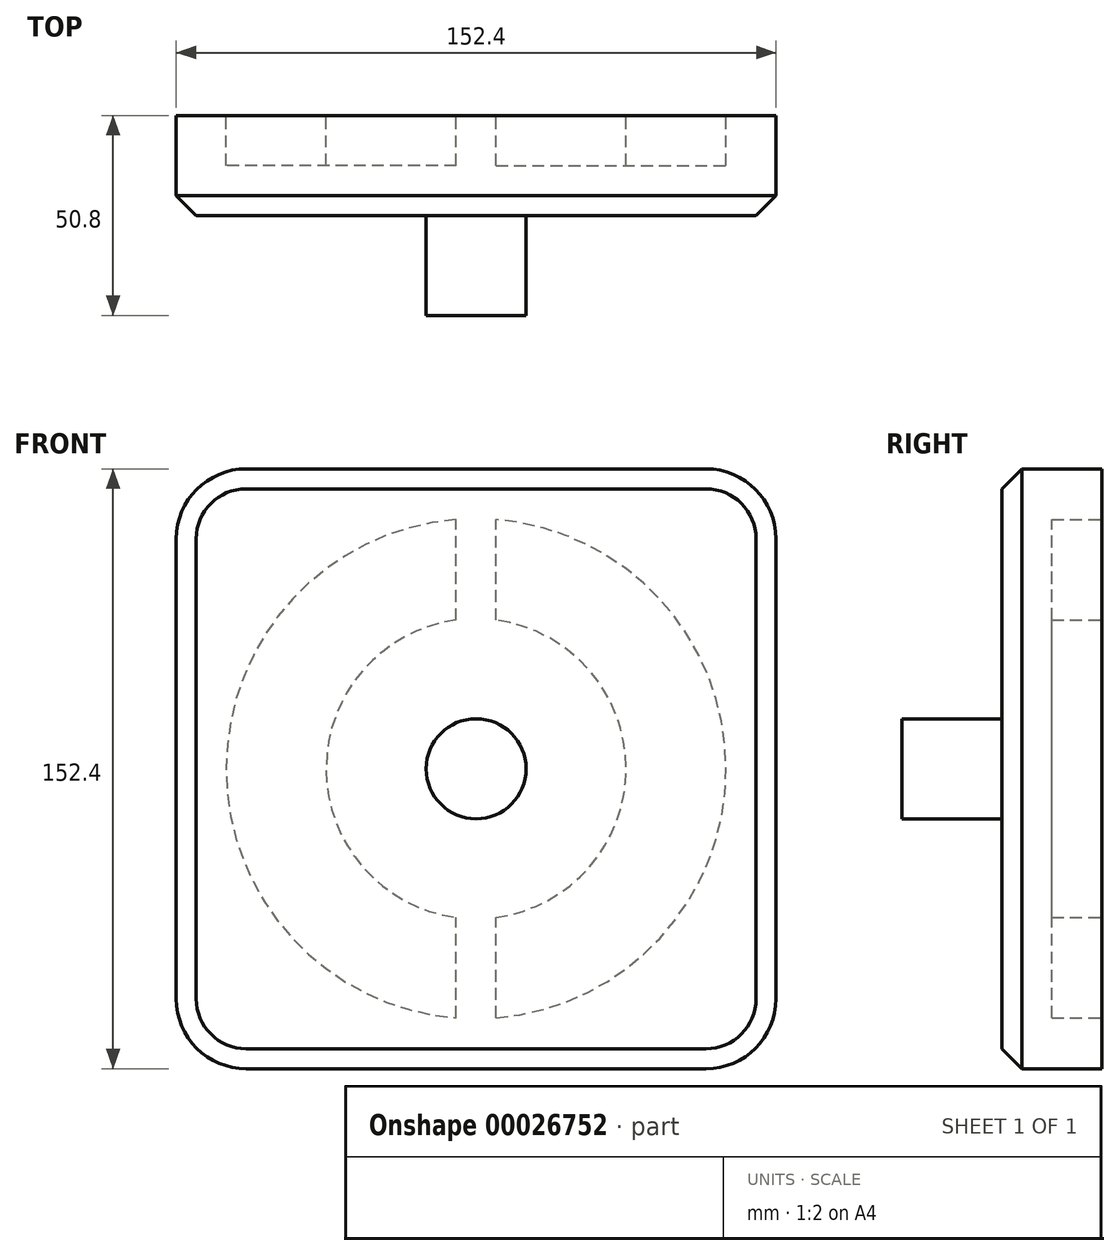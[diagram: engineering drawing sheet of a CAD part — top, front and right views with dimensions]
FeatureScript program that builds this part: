
annotation { "Feature Type Name" : "Feature", "Feature Type Description" : "" }
export const myFeature = defineFeature(function(context is Context, id is Id, definition is map)
    precondition{}
    {
        {
            var Q0;
            Q0=qCreatedBy(makeId("Front.planeOp"),FACE);
            var sketch = newSketch(context, id + "F0", { "sketchPlane" : qUnion([Q0])});
            skLineSegment(sketch, "E0.rect.bottom", {"start": v(76.2, -76.2) * mm, "end": v(-76.2, -76.2) * mm});
            skLineSegment(sketch, "E0.rect.top", {"start": v(76.2, 76.2) * mm, "end": v(-76.2, 76.2) * mm});
            skLineSegment(sketch, "E0.rect.left", {"start": v(76.2, -76.2) * mm, "end": v(76.2, 76.2) * mm});
            skLineSegment(sketch, "E0.rect.right", {"start": v(-76.2, -76.2) * mm, "end": v(-76.2, 76.2) * mm});
            skPoint(sketch, "E0.rect.middle", {"position": v(0, 0) * mm});
            skSolve(sketch);
        }
        {
            var Q0;
            Q0=makeQuery(id+"F0.imprint","IMPRINT",FACE,{"disambiguationData":[TD([[makeQuery(id+"F0.imprint","IMPRINT",EDGE,{"derivedFrom":sQuery(id+"F0.wireOp",EDGE,"E0.rect.bottom")}),-1.0]])]});
            extrude(context, id + "F1", {"entities" : qUnion([Q0]), "depth" : 25.4 * mm});
        }
        {
            var Q0;
            Q0=makeQuery(id+"F1.opExtrude","CAP_FACE",FACE,{"disambiguationData":[OSD([sQuery(id+"F0.wireOp",EDGE,"E0.rect.bottom"),sQuery(id+"F0.wireOp",EDGE,"E0.rect.top"),sQuery(id+"F0.wireOp",EDGE,"E0.rect.left"),sQuery(id+"F0.wireOp",EDGE,"E0.rect.right")])],"isStart":false});
            var sketch = newSketch(context, id + "F2", { "sketchPlane" : qUnion([Q0])});
            skCircle(sketch, "E1", {"center": v(0, 0) * mm, "radius": 12.7 * mm});
            skSolve(sketch);
        }
        {
            var Q0;
            Q0=makeQuery(id+"F2.imprint","IMPRINT",FACE,{"disambiguationData":[TD([[makeQuery(id+"F2.imprint","IMPRINT",EDGE,{"derivedFrom":sQuery(id+"F2.wireOp",EDGE,"E1")}),1.0]])]});
            extrude(context, id + "F3", {"entities" : qUnion([Q0]), "operationType" : NewBodyOperationType.ADD, "depth" : 25.4 * mm});
        }
        {
            var Q0;
            Q0=makeQuery(id+"F1.opExtrude","SWEPT_EDGE",EDGE,{"disambiguationData":[OSD([sQuery(id+"F0.wireOp",EDGE,"E0.rect.top"),sQuery(id+"F0.wireOp",EDGE,"E0.rect.left")])]});
            var Q1;
            Q1=makeQuery(id+"F1.opExtrude","SWEPT_EDGE",EDGE,{"disambiguationData":[OSD([sQuery(id+"F0.wireOp",EDGE,"E0.rect.top"),sQuery(id+"F0.wireOp",EDGE,"E0.rect.right")])]});
            var Q2;
            Q2=makeQuery(id+"F1.opExtrude","SWEPT_EDGE",EDGE,{"disambiguationData":[OSD([sQuery(id+"F0.wireOp",EDGE,"E0.rect.bottom"),sQuery(id+"F0.wireOp",EDGE,"E0.rect.left")])]});
            var Q3;
            Q3=makeQuery(id+"F1.opExtrude","SWEPT_EDGE",EDGE,{"disambiguationData":[OSD([sQuery(id+"F0.wireOp",EDGE,"E0.rect.bottom"),sQuery(id+"F0.wireOp",EDGE,"E0.rect.right")])]});
            fillet(context, id + "F4", {"entities" : qUnion([Q0, Q1, Q2, Q3]), "radius" : 17.78 * mm, "tangentPropagation" : true, "allowEdgeOverflow" : false});
        }
        {
            var Q0;
            Q0=makeQuery(id+"F1.opExtrude","CAP_EDGE",EDGE,{"disambiguationData":[OSD([sQuery(id+"F0.wireOp",EDGE,"E0.rect.top")])],"isStart":false});
            chamfer(context, id + "F5", {"entities" : qUnion([Q0]), "width" : 5.08 * mm, "tangentPropagation" : true});
        }
        {
            var Q0;
            Q0=makeQuery(id+"F1.opExtrude","CAP_FACE",FACE,{"disambiguationData":[OSD([sQuery(id+"F0.wireOp",EDGE,"E0.rect.bottom"),sQuery(id+"F0.wireOp",EDGE,"E0.rect.top"),sQuery(id+"F0.wireOp",EDGE,"E0.rect.left"),sQuery(id+"F0.wireOp",EDGE,"E0.rect.right")])],"isStart":true});
            var sketch = newSketch(context, id + "F6", { "sketchPlane" : qUnion([Q0])});
            skArc(sketch, "E2", {"start": v(-5.08, 63.3) * mm, "mid": v(-63.5, 0) * mm, "end": v(-5.08, -63.3) * mm});
            skLineSegment(sketch, "E3.rect.bottom", {"start": v(5.08, -76.2) * mm, "end": v(-5.08, -76.2) * mm});
            skLineSegment(sketch, "E3.rect.top", {"start": v(5.08, 76.2) * mm, "end": v(-5.08, 76.2) * mm});
            skLineSegment(sketch, "E3.rect.left", {"start": v(5.08, -63.3) * mm, "end": v(5.08, -37.76) * mm});
            skLineSegment(sketch, "E3.rect.right", {"start": v(-5.08, -63.3) * mm, "end": v(-5.08, -37.76) * mm});
            skArc(sketch, "E4", {"start": v(-5.08, 37.76) * mm, "mid": v(-38.1, 0) * mm, "end": v(-5.08, -37.76) * mm});
            skLineSegment(sketch, "E5.trimOffspring", {"start": v(-5.08, 37.76) * mm, "end": v(-5.08, 63.3) * mm});
            skLineSegment(sketch, "E6.trimOffspring", {"start": v(5.08, 37.76) * mm, "end": v(5.08, 63.3) * mm});
            skArc(sketch, "E7.trimOffspring", {"start": v(5.08, -37.76) * mm, "mid": v(38.1, 0) * mm, "end": v(5.08, 37.76) * mm});
            skArc(sketch, "E8.trimOffspring", {"start": v(5.08, -63.3) * mm, "mid": v(63.5, 0) * mm, "end": v(5.08, 63.3) * mm});
            skSolve(sketch);
        }
        {
            var Q0;
            Q0=makeQuery(id+"F6.imprint","IMPRINT",FACE,{"disambiguationData":[TD([[makeQuery(id+"F6.imprint","IMPRINT",EDGE,{"derivedFrom":sQuery(id+"F6.wireOp",EDGE,"E2")}),1.0]])]});
            var Q1;
            Q1=makeQuery(id+"F6.imprint","IMPRINT",FACE,{"disambiguationData":[TD([[makeQuery(id+"F6.imprint","IMPRINT",EDGE,{"derivedFrom":sQuery(id+"F6.wireOp",EDGE,"E3.rect.left")}),-1.0]])]});
            extrude(context, id + "F7", {"entities" : qUnion([Q0, Q1]), "operationType" : NewBodyOperationType.REMOVE, "oppositeDirection" : true, "depth" : 12.7 * mm});
        }
    });
